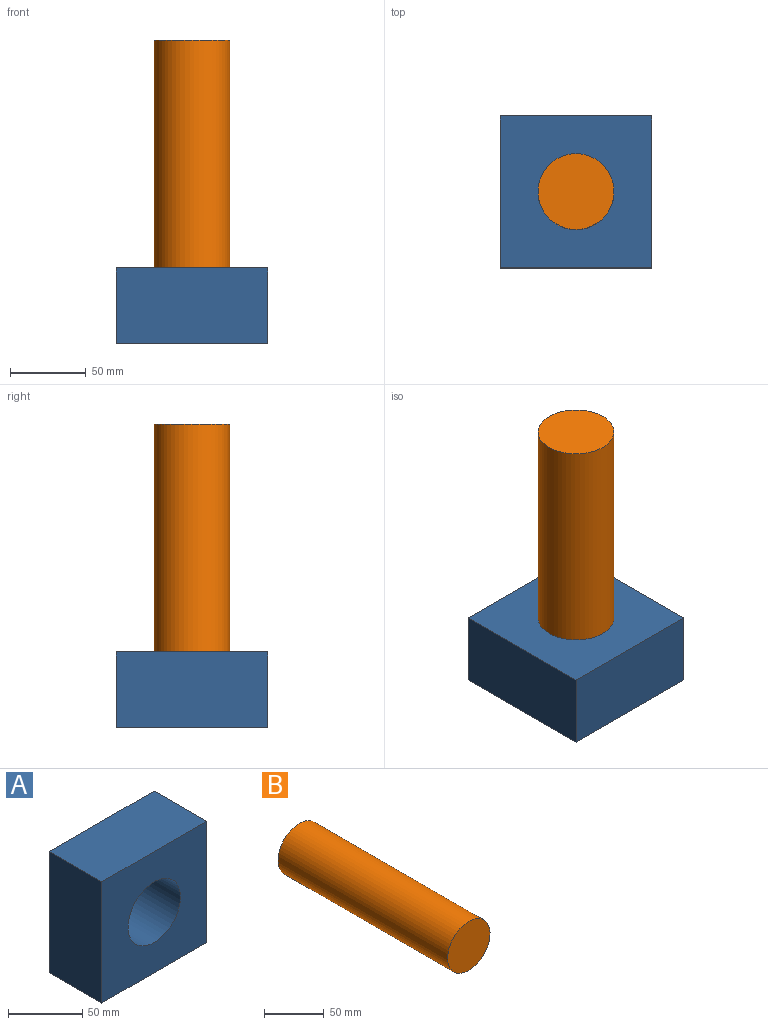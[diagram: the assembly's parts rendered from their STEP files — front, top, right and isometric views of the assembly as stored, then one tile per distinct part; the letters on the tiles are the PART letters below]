
ASSEMBLY  parts=2 mates=1
PART A: 7 faces, bbox 100x50x100 mm
  f0: plane 100x50mm, normal (-1,0,0), area 5000mm2, adj f1,f3,f4,f5
  f1: plane 100x50mm, normal (0,0,-1), area 5000mm2, adj f0,f2,f4,f5
  f2: plane 100x50mm, normal (1,0,0), area 5000mm2, adj f1,f3,f4,f5
  f3: plane 100x50mm, normal (0,0,1), area 5000mm2, adj f0,f2,f4,f5
  f4: plane 100x100mm, normal (0,-1,0), area 8036.5mm2, adj f0,f1,f2,f3,f6
  f5: plane 100x100mm, normal (0,1,0), area 8036.5mm2, adj f0,f1,f2,f3,f6
  f6: cylinder r=25mm len=50mm, axis (0,-1,0), area 7854mm2, adj f4,f5
PART B: 3 faces, bbox 50x200x50 mm
  f0: cylinder r=25mm len=200mm, axis (0,1,0), area 31415.9mm2, adj f1,f2
  f1: plane 50x50mm, normal (0,-1,0), area 1963.5mm2, adj f0
  f2: plane 50x50mm, normal (0,1,0), area 1963.5mm2, adj f0
PLACE A rot(axis=(-1,0,0),90deg) t=(0,0,0)mm
PLACE B rot(axis=(1,0,0),90deg) t=(0,0,250)mm
MATE slider A.f6 <-> B.f0  axis (0,0,-1) through (0,0,0)mm
